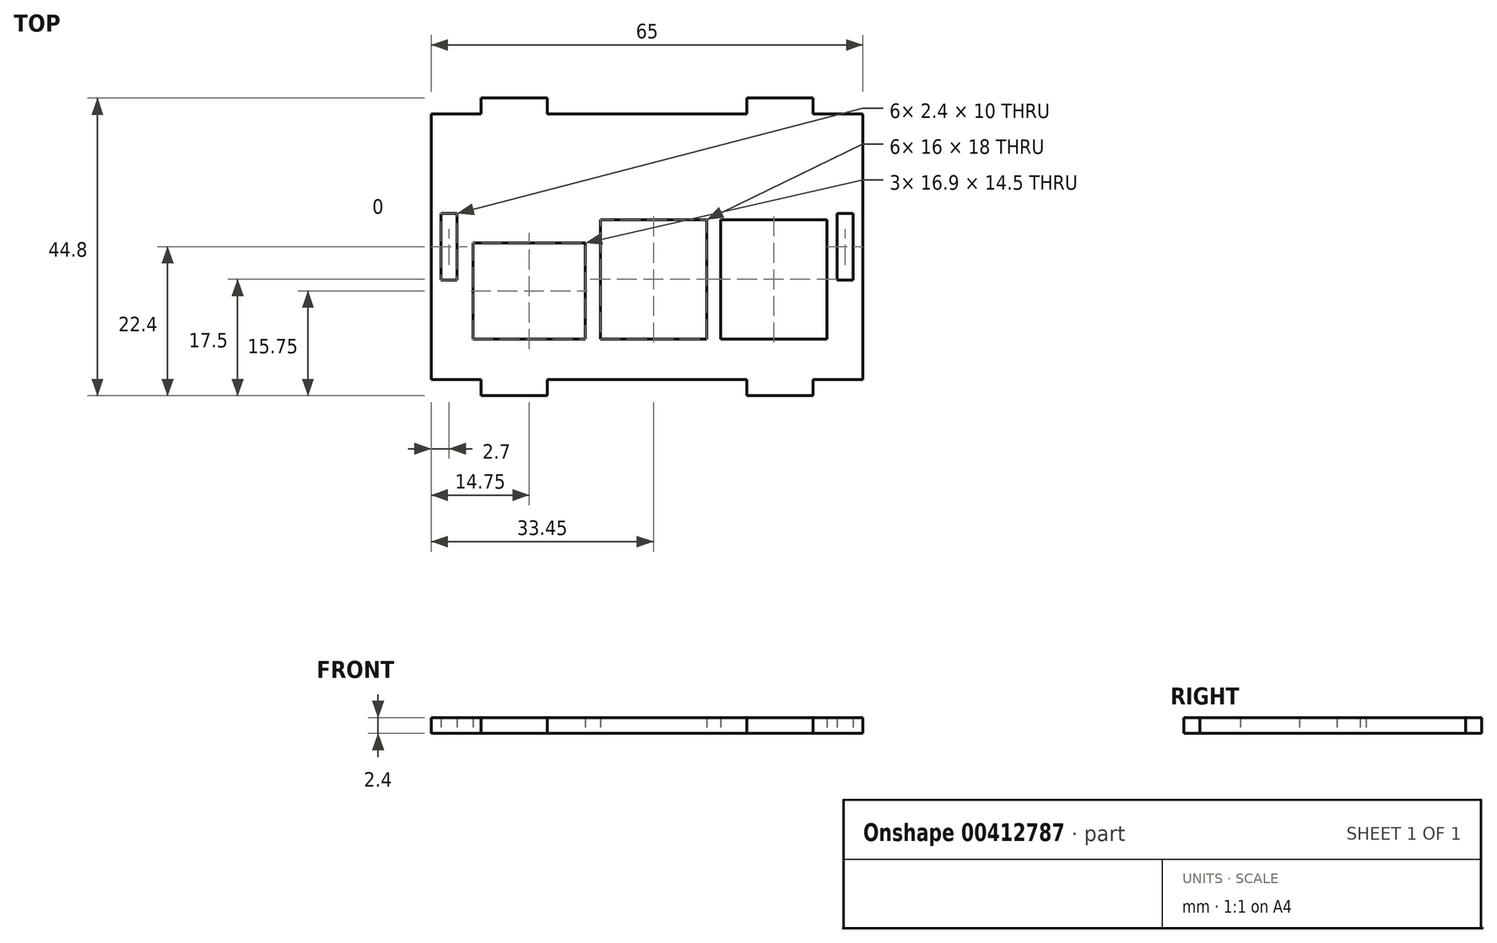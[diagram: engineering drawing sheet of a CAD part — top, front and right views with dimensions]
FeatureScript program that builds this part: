
annotation { "Feature Type Name" : "Feature", "Feature Type Description" : "" }
export const myFeature = defineFeature(function(context is Context, id is Id, definition is map)
    precondition{}
    {
        {
            var Q0;
            Q0=qCreatedBy(makeId("Top.planeOp"),FACE);
            var sketch = newSketch(context, id + "F0", { "sketchPlane" : qUnion([Q0])});
            skLineSegment(sketch, "E0.bottom", {"start": v(32.5, 20) * mm, "end": v(25, 20) * mm});
            skLineSegment(sketch, "E0.top", {"start": v(32.5, -20) * mm, "end": v(25, -20) * mm});
            skLineSegment(sketch, "E0.left", {"start": v(32.5, 20) * mm, "end": v(32.5, -20) * mm});
            skLineSegment(sketch, "E0.right", {"start": v(-32.5, 20) * mm, "end": v(-32.5, -20) * mm});
            skPoint(sketch, "E0.middle", {"position": v(0, 0) * mm});
            skLineSegment(sketch, "E1.bottom", {"start": v(-15, 22.4) * mm, "end": v(-25, 22.4) * mm});
            skLineSegment(sketch, "E1.left", {"start": v(-15, 22.4) * mm, "end": v(-15, 20) * mm});
            skLineSegment(sketch, "E1.right", {"start": v(-25, 22.4) * mm, "end": v(-25, 20) * mm});
            skPoint(sketch, "E1.middle", {"position": v(-20, 20) * mm});
            skLineSegment(sketch, "E2.bottom", {"start": v(25, 22.4) * mm, "end": v(15, 22.4) * mm});
            skLineSegment(sketch, "E2.left", {"start": v(25, 22.4) * mm, "end": v(25, 20) * mm});
            skLineSegment(sketch, "E2.right", {"start": v(15, 22.4) * mm, "end": v(15, 20) * mm});
            skPoint(sketch, "E2.middle", {"position": v(20, 20) * mm});
            skLineSegment(sketch, "E3.top", {"start": v(-15, -22.4) * mm, "end": v(-25, -22.4) * mm});
            skLineSegment(sketch, "E3.left", {"start": v(-15, -20) * mm, "end": v(-15, -22.4) * mm});
            skLineSegment(sketch, "E3.right", {"start": v(-25, -20) * mm, "end": v(-25, -22.4) * mm});
            skPoint(sketch, "E3.middle", {"position": v(-20, -20) * mm});
            skLineSegment(sketch, "E4.top", {"start": v(25, -22.4) * mm, "end": v(15, -22.4) * mm});
            skLineSegment(sketch, "E4.left", {"start": v(25, -20) * mm, "end": v(25, -22.4) * mm});
            skLineSegment(sketch, "E4.right", {"start": v(15, -20) * mm, "end": v(15, -22.4) * mm});
            skPoint(sketch, "E4.middle", {"position": v(20, -20) * mm});
            skPoint(sketch, "E5.middle", {"position": v(0, -20) * mm});
            skLineSegment(sketch, "E6.trimOffspring", {"start": v(-25, 20) * mm, "end": v(-32.5, 20) * mm});
            skLineSegment(sketch, "E7.trimOffspring", {"start": v(15, 20) * mm, "end": v(-15, 20) * mm});
            skLineSegment(sketch, "E8.trimOffspring", {"start": v(15, -20) * mm, "end": v(7.5, -20) * mm});
            skLineSegment(sketch, "E9.trimOffspring", {"start": v(7.5, -20) * mm, "end": v(-15, -20) * mm});
            skLineSegment(sketch, "E10.trimOffspring", {"start": v(-25, -20) * mm, "end": v(-32.5, -20) * mm});
            skLineSegment(sketch, "E11.bottom", {"start": v(-28.6, 5) * mm, "end": v(-31, 5) * mm});
            skLineSegment(sketch, "E11.top", {"start": v(-28.6, -5) * mm, "end": v(-31, -5) * mm});
            skLineSegment(sketch, "E11.left", {"start": v(-28.6, 5) * mm, "end": v(-28.6, -5) * mm});
            skLineSegment(sketch, "E11.right", {"start": v(-31, 5) * mm, "end": v(-31, -5) * mm});
            skPoint(sketch, "E11.middle", {"position": v(-29.8, 0) * mm});
            skLineSegment(sketch, "E12.bottom", {"start": v(31, 5) * mm, "end": v(28.6, 5) * mm});
            skLineSegment(sketch, "E12.top", {"start": v(31, -5) * mm, "end": v(28.6, -5) * mm});
            skLineSegment(sketch, "E12.left", {"start": v(31, 5) * mm, "end": v(31, -5) * mm});
            skLineSegment(sketch, "E12.right", {"start": v(28.6, 5) * mm, "end": v(28.6, -5) * mm});
            skPoint(sketch, "E12.middle", {"position": v(29.8, 0) * mm});
            skLineSegment(sketch, "E13.bottom", {"start": v(-26.2, 0.6) * mm, "end": v(-9.3, 0.6) * mm});
            skLineSegment(sketch, "E13.top", {"start": v(-26.2, -13.9) * mm, "end": v(-9.3, -13.9) * mm});
            skLineSegment(sketch, "E13.left", {"start": v(-26.2, 0.6) * mm, "end": v(-26.2, -13.9) * mm});
            skLineSegment(sketch, "E13.right", {"start": v(-9.3, 0.6) * mm, "end": v(-9.3, -13.9) * mm});
            skLineSegment(sketch, "E14.bottom", {"start": v(-7.05, 4.1) * mm, "end": v(8.95, 4.1) * mm});
            skLineSegment(sketch, "E14.top", {"start": v(-7.05, -13.9) * mm, "end": v(8.95, -13.9) * mm});
            skLineSegment(sketch, "E14.left", {"start": v(-7.05, 4.1) * mm, "end": v(-7.05, -13.9) * mm});
            skLineSegment(sketch, "E14.right", {"start": v(8.95, 4.1) * mm, "end": v(8.95, -13.9) * mm});
            skLineSegment(sketch, "E15.bottom", {"start": v(11.05, 4.1) * mm, "end": v(27.05, 4.1) * mm});
            skLineSegment(sketch, "E15.top", {"start": v(11.05, -13.9) * mm, "end": v(27.05, -13.9) * mm});
            skLineSegment(sketch, "E15.left", {"start": v(11.05, 4.1) * mm, "end": v(11.05, -13.9) * mm});
            skLineSegment(sketch, "E15.right", {"start": v(27.05, 4.1) * mm, "end": v(27.05, -13.9) * mm});
            skSolve(sketch);
        }
        {
            var Q0;
            Q0=qSketchRegion(id+"F0",true);
            extrude(context, id + "F1", {"entities" : qUnion([Q0]), "depth" : 2.4 * mm});
        }
    });
